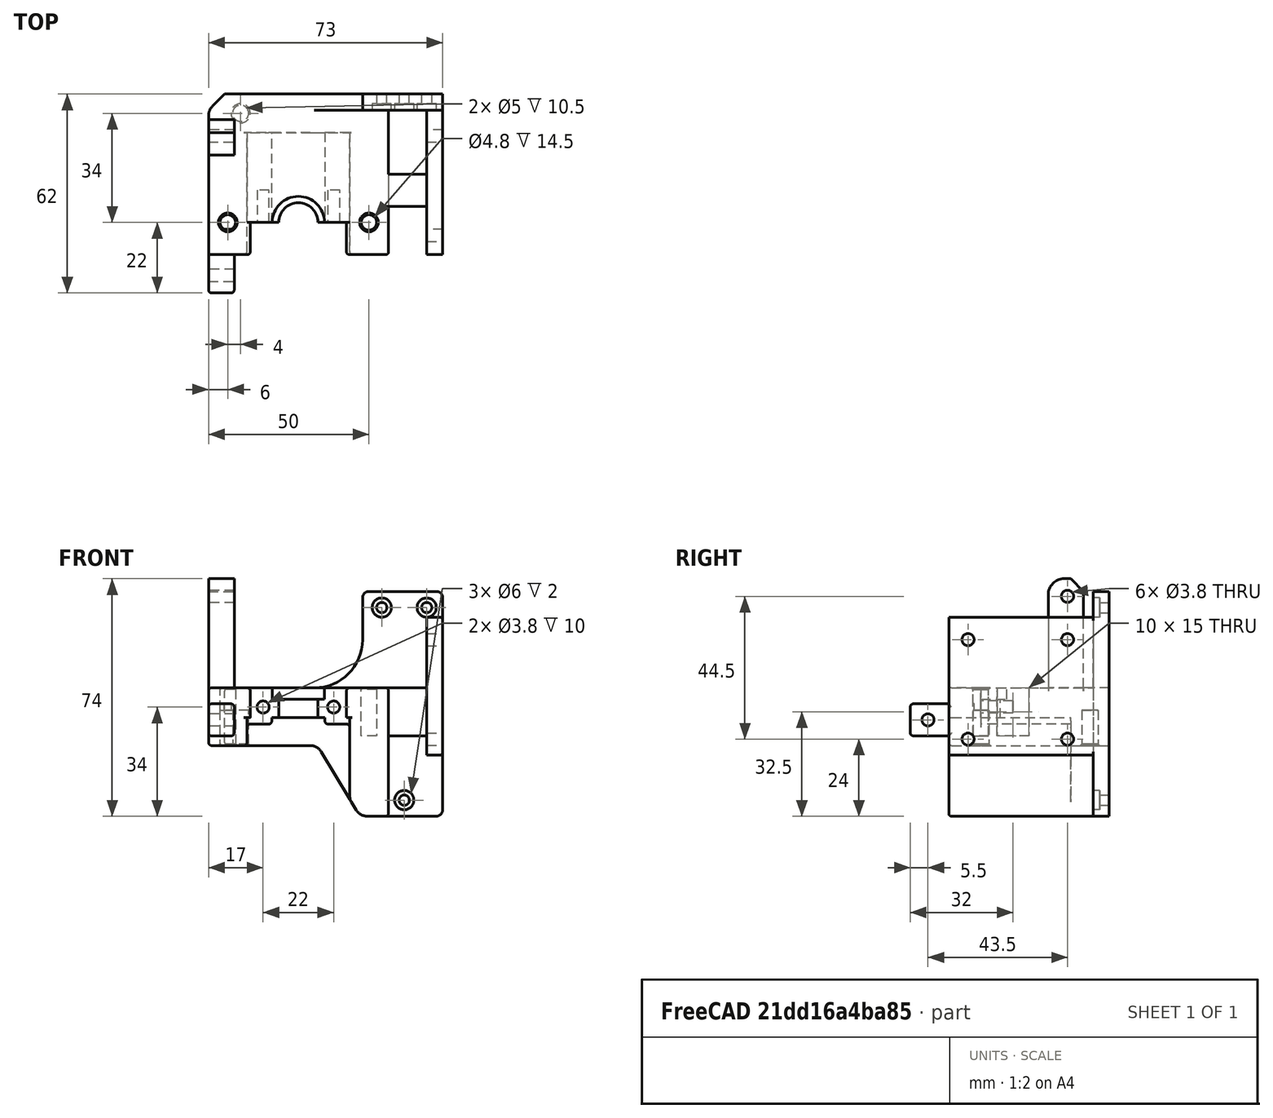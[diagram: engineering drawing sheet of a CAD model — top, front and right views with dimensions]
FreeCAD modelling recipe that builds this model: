
FCSTD DOCUMENT  (FreeCAD 0.19R)
Label: head8
License: All rights reserved
LicenseURL: http://en.wikipedia.org/wiki/All_rights_reserved
objects: Sketcher::SketchObject×19, PartDesign::Pocket×15, PartDesign::Fillet×15, PartDesign::Pad×4, PartDesign::Chamfer×4, PartDesign::Body×1, Mesh::Feature×1
note: 96 computed .brp shape members not serialized (recipe doc carries the construction recipe); baked Part::Feature solids carry a one-line shape summary decoded from their .brp

FEATURE [Sketcher::SketchObject] Sketch
  FullyConstrained = true
  MapMode = 5
  Support = -> [XY_Plane]
  sketch-geometry (5):
    g0: LineSegment StartX=0 StartY=0 StartZ=0 EndX=45 EndY=0 EndZ=0
    g1: LineSegment StartX=-28 StartY=0 StartZ=0 EndX=0 EndY=0 EndZ=0
    g2: LineSegment StartX=-28 StartY=0 StartZ=0 EndX=-28 EndY=-50 EndZ=0
    g3: LineSegment StartX=-28 StartY=-50 StartZ=0 EndX=45 EndY=-50 EndZ=0
    g4: LineSegment StartX=45 StartY=-50 StartZ=0 EndX=45 EndY=0 EndZ=0
  constraints (14):
    c: Coincident(g-1,g0)
    c: PointOnObject(g0,g-1)
    c: PointOnObject(g1,g-1)
    c: Coincident(g1,g0)
    c: Coincident(g1,g2)
    c: Vertical(g2)
    c: Coincident(g2,g3)
    c: Horizontal(g3)
    c: Coincident(g3,g4)
    c: Coincident(g4,g0)
    c: Vertical(g4)
    c: Distance(g4) = 50
    c: DistanceX(g0) = 45
    c: DistanceX(g1) = -28
FEATURE [PartDesign::Pad] Pad
  Direction = (1,1,1)
  Length = 70
  Length2 = 100
  Profile = -> Sketch
  Type = 0
FEATURE [Sketcher::SketchObject] Sketch001
  FullyConstrained = false
  MapMode = 5
  Placement = pos=(0,0,70) rot=(0,0,1;0rad)
  Support = -> [Pad]
  sketch-geometry (4):
    g0: LineSegment StartX=28.1122 StartY=-5 StartZ=0 EndX=40 EndY=-5 EndZ=0
    g1: LineSegment StartX=40 StartY=-5 StartZ=0 EndX=40 EndY=-51.78 EndZ=0
    g2: LineSegment StartX=40 StartY=-51.78 StartZ=0 EndX=28.1122 EndY=-51.78 EndZ=0
    g3: LineSegment StartX=28.1122 StartY=-51.78 StartZ=0 EndX=28.1122 EndY=-5 EndZ=0
  constraints (11):
    c: Coincident(g0,g1)
    c: Coincident(g1,g2)
    c: Coincident(g2,g3)
    c: Coincident(g3,g0)
    c: Horizontal(g0)
    c: Horizontal(g2)
    c: Vertical(g1)
    c: Vertical(g3)
    c: DistanceX(g0) = 40
    c: DistanceY(g1) = -51.78
    c: DistanceY(g0) = -5
FEATURE [PartDesign::Pocket] Pocket  label="BOBnotch"
  BaseFeature = -> Pad
  Length = 5
  Length2 = 100
  Profile = -> Sketch001
  Type = 1
FEATURE [Sketcher::SketchObject] Sketch002
  FullyConstrained = false
  MapMode = 5
  Placement = pos=(0,0,70) rot=(0,0,1;0rad)
  Support = -> [Pocket]
  sketch-geometry (6):
    g0: LineSegment StartX=30 StartY=-5 StartZ=0 EndX=30 EndY=-65.096 EndZ=0
    g1: LineSegment StartX=30 StartY=-65.096 StartZ=0 EndX=-40.7834 EndY=-65.096 EndZ=0
    g2: LineSegment StartX=-40.7834 StartY=-65.096 StartZ=0 EndX=-40.7834 EndY=12.9948 EndZ=0
    g3: LineSegment StartX=-40.7834 StartY=12.9948 StartZ=0 EndX=20 EndY=12.9948 EndZ=0
    g4: LineSegment StartX=20 StartY=12.9948 StartZ=0 EndX=20 EndY=-5 EndZ=0
    g5: LineSegment StartX=20 StartY=-5 StartZ=0 EndX=30 EndY=-5 EndZ=0
  constraints (15):
    c: Coincident(g0,g1)
    c: Coincident(g1,g2)
    c: Horizontal(g1)
    c: Vertical(g0)
    c: Vertical(g2)
    c: DistanceX(g0) = 30
    c: DistanceY(g0) = -5
    c: Coincident(g2,g3)
    c: Horizontal(g3)
    c: Coincident(g3,g4)
    c: Coincident(g4,g5)
    c: Coincident(g5,g0)
    c: Horizontal(g5)
    c: Vertical(g4)
    c: DistanceX(g3) = 20
FEATURE [PartDesign::Pocket] Pocket001  label="stepperplatform"
  BaseFeature = -> Pocket
  Length = 30
  Length2 = 100
  Profile = -> Sketch002
  Type = 0
FEATURE [Sketcher::SketchObject] Sketch003
  FullyConstrained = true
  MapMode = 5
  Placement = pos=(0,0,40) rot=(0,0,1;0rad)
  Support = -> [Pocket001]
  sketch-geometry (2):
    g0: Circle CenterX=-22 CenterY=-40 CenterZ=0 NormalX=0 NormalY=0 NormalZ=1 AngleXU=0 Radius=2.4
    g1: Circle CenterX=22 CenterY=-40 CenterZ=0 NormalX=0 NormalY=0 NormalZ=1 AngleXU=0 Radius=2.4
  constraints (5):
    c: Equal(g1,g0)
    c: Symmetric(g1,g0,g-2)
    c: Distance(g1,g0) = 44
    c: DistanceY(g0) = -40
    c: Diameter(g1) = 4.8
FEATURE [PartDesign::Pocket] Pocket002  label="steppermountholes"
  BaseFeature = -> Pocket001
  Length = 15
  Length2 = 100
  Profile = -> Sketch003
  Type = 0
FEATURE [Sketcher::SketchObject] Sketch004
  FullyConstrained = true
  MapMode = 5
  Placement = pos=(0,0,40) rot=(0,0,1;0rad)
  Support = -> [Pocket002]
  sketch-geometry (4):
    g0: ArcOfCircle CenterX=0 CenterY=-40 CenterZ=0 NormalX=0 NormalY=0 NormalZ=1 AngleXU=0 Radius=8.125 StartAngle=4e-16 EndAngle=3.14159
    g1: LineSegment StartX=8.125 StartY=-40 StartZ=0 EndX=8.125 EndY=-59.24 EndZ=0
    g2: LineSegment StartX=8.125 StartY=-59.24 StartZ=0 EndX=-8.125 EndY=-59.24 EndZ=0
    g3: LineSegment StartX=-8.125 StartY=-59.24 StartZ=0 EndX=-8.125 EndY=-40 EndZ=0
  constraints (11):
    c: PointOnObject(g0,g-2)
    c: Diameter(g0) = 16.25
    c: DistanceY(g0) = -40
    c: Coincident(g1,g2)
    c: Coincident(g2,g3)
    c: Horizontal(g2)
    c: Vertical(g3)
    c: Distance(g3) = 19.24
    c: Tangent(g3,g0) = 1.5708
    c: Tangent(g1,g0) = 1.5708
    c: Vertical(g1)
FEATURE [PartDesign::Pocket] Pocket003  label="hotendnotch001"
  BaseFeature = -> Pocket002
  Length = 3.5
  Length2 = 100
  Profile = -> Sketch004
  Type = 0
FEATURE [Sketcher::SketchObject] Sketch018
  FullyConstrained = true
  MapMode = 5
  Placement = pos=(0,0,36.5) rot=(0,0,1;0rad)
  sketch-geometry (4):
    g0: ArcOfCircle CenterX=0 CenterY=-40 CenterZ=0 NormalX=0 NormalY=0 NormalZ=1 AngleXU=0 Radius=6.1 StartAngle=-4e-14 EndAngle=3.14159
    g1: LineSegment StartX=6.1 StartY=-40 StartZ=0 EndX=6.1 EndY=-50 EndZ=0
    g2: LineSegment StartX=-6.1 StartY=-40 StartZ=0 EndX=-6.1 EndY=-50 EndZ=0
    g3: LineSegment StartX=6.1 StartY=-50 StartZ=0 EndX=-6.1 EndY=-50 EndZ=0
  constraints (11):
    c: PointOnObject(g0,g-2)
    c: Vertical(g1)
    c: Vertical(g2)
    c: Coincident(g3,g1)
    c: Coincident(g3,g2)
    c: Tangent(g1,g0) = 1.5708
    c: Tangent(g2,g0) = -1.5708
    c: DistanceY(g0) = -40
    c: Diameter(g0) = 12.2
    c: Horizontal(g3)
    c: Distance(g1) = 10
FEATURE [PartDesign::Pocket] Pocket004
  BaseFeature = -> Pocket003
  Length = 9
  Length2 = 100
  Profile = -> Sketch018
  Type = 0
FEATURE [Sketcher::SketchObject] Sketch021
  FullyConstrained = false
  MapMode = 5
  Placement = pos=(0,-50,0) rot=(1,0,0;1.5708rad)
  Support = -> [Pocket004]
  sketch-geometry (4):
    g0: LineSegment StartX=-15 StartY=43.4175 StartZ=0 EndX=15 EndY=43.4175 EndZ=0
    g1: LineSegment StartX=15 StartY=43.4175 StartZ=0 EndX=15 EndY=-9.74423 EndZ=0
    g2: LineSegment StartX=15 StartY=-9.74423 StartZ=0 EndX=-15 EndY=-9.74423 EndZ=0
    g3: LineSegment StartX=-15 StartY=-9.74423 StartZ=0 EndX=-15 EndY=43.4175 EndZ=0
  constraints (9):
    c: Coincident(g0,g1)
    c: Coincident(g1,g2)
    c: Coincident(g2,g3)
    c: Coincident(g3,g0)
    c: Horizontal(g2)
    c: Vertical(g1)
    c: Vertical(g3)
    c: Distance(g0,g0) = 30
    c: Symmetric(g0,g0,g-2)
FEATURE [PartDesign::Pocket] Pocket005  label="clampnotch"
  BaseFeature = -> Pocket004
  Length = 10
  Length2 = 100
  Profile = -> Sketch021
  Type = 0
FEATURE [Sketcher::SketchObject] Sketch022
  ExternalGeometry = -> [Pocket005]
  FullyConstrained = false
  MapMode = 5
  Placement = pos=(0,-50,0) rot=(1,0,0;1.5708rad)
  Support = -> [Pocket005]
  sketch-geometry (4):
    g0: LineSegment StartX=-16 StartY=30.7 StartZ=0 EndX=16 EndY=30.7 EndZ=0
    g1: LineSegment StartX=16 StartY=30.7 StartZ=0 EndX=16 EndY=-27.9602 EndZ=0
    g2: LineSegment StartX=16 StartY=-27.9602 StartZ=0 EndX=-16 EndY=-27.9602 EndZ=0
    g3: LineSegment StartX=-16 StartY=-27.9602 StartZ=0 EndX=-16 EndY=30.7 EndZ=0
  constraints (10):
    c: Coincident(g0,g1)
    c: Coincident(g1,g2)
    c: Coincident(g2,g3)
    c: Coincident(g3,g0)
    c: Horizontal(g2)
    c: Vertical(g1)
    c: Vertical(g3)
    c: Symmetric(g0,g0,g-2)
    c: Distance(g0) = 32
    c: Distance(g-5,g0) = 5.8
FEATURE [PartDesign::Pocket] Pocket006  label="fanNotch"
  BaseFeature = -> Pocket005
  Length = 38
  Length2 = 100
  Profile = -> Sketch022
  Type = 0
FEATURE [Sketcher::SketchObject] Sketch023
  ExternalGeometry = -> [Pocket006]
  FullyConstrained = true
  MapMode = 5
  Placement = pos=(0,-50,0) rot=(1,0,0;1.5708rad)
  Support = -> [Pocket006]
  sketch-geometry (4):
    g0: LineSegment StartX=-38.33 StartY=22 StartZ=0 EndX=6 EndY=22 EndZ=0
    g1: LineSegment StartX=6 StartY=22 StartZ=0 EndX=24 EndY=-8 EndZ=0
    g2: LineSegment StartX=24 StartY=-8 StartZ=0 EndX=-38.33 EndY=-8 EndZ=0
    g3: LineSegment StartX=-38.33 StartY=-8 StartZ=0 EndX=-38.33 EndY=22 EndZ=0
  constraints (12):
    c: Horizontal(g0)
    c: Coincident(g0,g1)
    c: Coincident(g1,g2)
    c: Horizontal(g2)
    c: Coincident(g2,g3)
    c: Coincident(g3,g0)
    c: DistanceX(g0) = 6
    c: DistanceX(g1) = 24
    c: DistanceY(g1) = -8
    c: Vertical(g3)
    c: Distance(g0) = 44.33
    c: Distance(g-3,g0) = 18
FEATURE [PartDesign::Pocket] Pocket007
  BaseFeature = -> Pocket006
  Length = 51
  Length2 = 100
  Profile = -> Sketch023
  Type = 0
FEATURE [Sketcher::SketchObject] Sketch008
  FullyConstrained = false
  MapMode = 5
  Placement = pos=(0,-50,0) rot=(1,0,0;1.5708rad)
  Support = -> [Pocket007]
  sketch-geometry (8):
    g0: LineSegment StartX=34.6158 StartY=72.6945 StartZ=0 EndX=53.669 EndY=72.6945 EndZ=0
    g1: LineSegment StartX=53.669 StartY=72.6945 StartZ=0 EndX=53.669 EndY=62 EndZ=0
    g2: LineSegment StartX=53.669 StartY=62 StartZ=0 EndX=34.6158 EndY=62 EndZ=0
    g3: LineSegment StartX=34.6158 StartY=62 StartZ=0 EndX=34.6158 EndY=72.6945 EndZ=0
    g4: LineSegment StartX=34.9227 StartY=19 StartZ=0 EndX=70.6727 EndY=19 EndZ=0
    g5: LineSegment StartX=70.6727 StartY=19 StartZ=0 EndX=70.6727 EndY=-17.1722 EndZ=0
    g6: LineSegment StartX=70.6727 StartY=-17.1722 StartZ=0 EndX=34.9227 EndY=-17.1722 EndZ=0
    g7: LineSegment StartX=34.9227 StartY=-17.1722 StartZ=0 EndX=34.9227 EndY=19 EndZ=0
  constraints (18):
    c: Coincident(g0,g1)
    c: Coincident(g1,g2)
    c: Coincident(g2,g3)
    c: Coincident(g3,g0)
    c: Horizontal(g0)
    c: Horizontal(g2)
    c: Vertical(g1)
    c: Vertical(g3)
    c: Coincident(g4,g5)
    c: Coincident(g5,g6)
    c: Coincident(g6,g7)
    c: Coincident(g7,g4)
    c: Horizontal(g4)
    c: Horizontal(g6)
    c: Vertical(g5)
    c: Vertical(g7)
    c: DistanceY(g2) = 62
    c: DistanceY(g4) = 19
FEATURE [PartDesign::Pocket] Pocket008
  BaseFeature = -> Pocket007
  Length = 45
  Length2 = 100
  Profile = -> Sketch008
  Type = 0
FEATURE [Sketcher::SketchObject] Sketch009
  FullyConstrained = true
  MapMode = 5
  Placement = pos=(45,0,0) rot=(0.57735,0.57735,0.57735;2.0944rad)
  Support = -> [Pocket008]
  sketch-geometry (5):
    g0: Circle CenterX=-44 CenterY=55 CenterZ=0 NormalX=0 NormalY=0 NormalZ=1 AngleXU=0 Radius=1.9
    g1: Circle CenterX=-13 CenterY=24 CenterZ=0 NormalX=0 NormalY=0 NormalZ=1 AngleXU=0 Radius=1.9
    g2: LineSegment StartX=-44 StartY=55 StartZ=0 EndX=-13 EndY=24 EndZ=0
    g3: Circle CenterX=-13 CenterY=55 CenterZ=0 NormalX=0 NormalY=0 NormalZ=1 AngleXU=0 Radius=1.9
    g4: Circle CenterX=-44 CenterY=24 CenterZ=0 NormalX=0 NormalY=0 NormalZ=1 AngleXU=0 Radius=1.9
  constraints (14):
    c: Coincident(g2,g0)
    c: Coincident(g2,g1)
    c: Angle(g2) = -0.785398
    c: DistanceX(g1) = -13
    c: DistanceY(g1) = 24
    c: Diameter(g4) = 3.8
    c: Equal(g4,g0)
    c: Equal(g4,g3)
    c: Equal(g4,g1)
    c: DistanceY(g4,g0) = 31
    c: DistanceX(g0,g3) = 31
    c: DistanceX(g4,g1) = 31
    c: DistanceY(g4) = 24
    c: DistanceY(g1,g3) = 31
FEATURE [PartDesign::Pocket] Pocket009  label="pcbholes"
  BaseFeature = -> Pocket008
  Length = 5
  Length2 = 100
  Profile = -> Sketch009
  Type = 0
FEATURE [Sketcher::SketchObject] Sketch015
  FullyConstrained = false
  MapMode = 5
  Placement = pos=(-28,0,0) rot=(0.57735,-0.57735,-0.57735;2.0944rad)
  Support = -> [Pocket009]
  sketch-geometry (8):
    g0: LineSegment StartX=8 StartY=74 StartZ=0 EndX=19 EndY=74 EndZ=0
    g1: LineSegment StartX=19 StartY=74 StartZ=0 EndX=19 EndY=35.8156 EndZ=0
    g2: LineSegment StartX=19 StartY=35.8156 StartZ=0 EndX=8 EndY=35.8156 EndZ=0
    g3: LineSegment StartX=8 StartY=35.8156 StartZ=0 EndX=8 EndY=74 EndZ=0
    g4: LineSegment StartX=42.1188 StartY=35 StartZ=0 EndX=62 EndY=35 EndZ=0
    g5: LineSegment StartX=62 StartY=35 StartZ=0 EndX=62 EndY=25 EndZ=0
    g6: LineSegment StartX=62 StartY=25 StartZ=0 EndX=42.1188 EndY=25 EndZ=0
    g7: LineSegment StartX=42.1188 StartY=25 StartZ=0 EndX=42.1188 EndY=35 EndZ=0
  constraints (22):
    c: Coincident(g0,g1)
    c: Coincident(g1,g2)
    c: Coincident(g2,g3)
    c: Coincident(g3,g0)
    c: Horizontal(g0)
    c: Horizontal(g2)
    c: Vertical(g1)
    c: Vertical(g3)
    c: DistanceY(g0) = 74
    c: Coincident(g4,g5)
    c: Coincident(g5,g6)
    c: Coincident(g6,g7)
    c: Coincident(g7,g4)
    c: Horizontal(g4)
    c: Horizontal(g6)
    c: Vertical(g5)
    c: Vertical(g7)
    c: DistanceX(g4) = 62
    c: DistanceY(g4) = 35
    c: DistanceY(g5) = 25
    c: DistanceX(g0) = 19
    c: DistanceX(g0) = 8
FEATURE [PartDesign::Pad] Pad001
  BaseFeature = -> Pocket009
  Direction = (1,1,1)
  Length = 8
  Length2 = 100
  Profile = -> Sketch015
  Reversed = true
  Type = 0
FEATURE [Sketcher::SketchObject] Sketch011
  FullyConstrained = true
  MapMode = 5
  Placement = pos=(-28,0,0) rot=(0.57735,-0.57735,-0.57735;2.0944rad)
  Support = -> [Pad001]
  sketch-geometry (3):
    g0: Circle CenterX=56.5 CenterY=30 CenterZ=0 NormalX=0 NormalY=0 NormalZ=1 AngleXU=0 Radius=1.9
    g1: Circle CenterX=13 CenterY=68.5 CenterZ=0 NormalX=0 NormalY=0 NormalZ=1 AngleXU=0 Radius=1.9
    g2: GeomPoint X=36 Y=48 Z=0
  constraints (8):
    c: Diameter(g0) = 3.8
    c: DistanceY(g0) = 30
    c: Diameter(g1) = 3.8
    c: DistanceX(g1) = 13
    c: DistanceY(g0,g2) = 18
    c: DistanceY(g2,g1) = 20.5
    c: DistanceX(g2,g0) = 20.5
    c: DistanceX(g1,g2) = 23
FEATURE [PartDesign::Pocket] Pocket010
  BaseFeature = -> Pad001
  Length = 10
  Length2 = 100
  Profile = -> Sketch011
  Type = 0
FEATURE [Sketcher::SketchObject] Sketch010
  FullyConstrained = true
  MapMode = 5
  Placement = pos=(0,0,0) rot=(0,0.707107,0.707107;3.14159rad)
  Support = -> [Pocket010]
  sketch-geometry (3):
    g0: Circle CenterX=-33 CenterY=5 CenterZ=0 NormalX=0 NormalY=0 NormalZ=1 AngleXU=0 Radius=1.6
    g1: Circle CenterX=-40 CenterY=65 CenterZ=0 NormalX=0 NormalY=0 NormalZ=1 AngleXU=0 Radius=1.6
    g2: Circle CenterX=-26 CenterY=65 CenterZ=0 NormalX=0 NormalY=0 NormalZ=1 AngleXU=0 Radius=1.6
  constraints (9):
    c: Diameter(g0) = 3.2
    c: Equal(g0,g2)
    c: Equal(g0,g1)
    c: DistanceX(g0) = -33
    c: Distance(g1,g2) = 14
    c: DistanceX(g2) = -26
    c: DistanceY(g0) = 5
    c: DistanceY(g2) = 65
    c: DistanceY(g1) = 65
FEATURE [PartDesign::Pocket] Pocket011
  BaseFeature = -> Pocket010
  Length = 7
  Length2 = 100
  Profile = -> Sketch010
  Type = 0
FEATURE [Sketcher::SketchObject] Sketch017
  FullyConstrained = false
  MapMode = 5
  Placement = pos=(0,-5,0) rot=(1,0,0;1.5708rad)
  Support = -> [Pocket011]
  sketch-geometry (3):
    g0: Circle CenterX=26 CenterY=65 CenterZ=0 NormalX=0 NormalY=0 NormalZ=1 AngleXU=0 Radius=3
    g1: Circle CenterX=33 CenterY=5 CenterZ=0 NormalX=0 NormalY=0 NormalZ=1 AngleXU=0 Radius=3
    g2: Circle CenterX=40 CenterY=65 CenterZ=0 NormalX=0 NormalY=0 NormalZ=1 AngleXU=0 Radius=3
  constraints (3):
    c: Diameter(g2) = 6
    c: Equal(g2,g1)
    c: Equal(g2,g0)
FEATURE [PartDesign::Pocket] Pocket012
  BaseFeature = -> Pocket011
  Length = 2
  Length2 = 100
  Profile = -> Sketch017
  Type = 0
FEATURE [Sketcher::SketchObject] Sketch013
  ExternalGeometry = -> [Pocket012]
  FullyConstrained = true
  MapMode = 5
  Placement = pos=(0,-40,5.3e-15) rot=(1,0,0;1.5708rad)
  Support = -> [Pocket012]
  sketch-geometry (2):
    g0: Circle CenterX=-11 CenterY=34 CenterZ=0 NormalX=0 NormalY=0 NormalZ=1 AngleXU=0 Radius=1.9
    g1: Circle CenterX=11 CenterY=34 CenterZ=0 NormalX=0 NormalY=0 NormalZ=1 AngleXU=0 Radius=1.9
  constraints (5):
    c: Symmetric(g1,g0,g-2)
    c: Distance(g1,g0) = 22
    c: Diameter(g1) = 3.8
    c: Equal(g1,g0)
    c: Distance(g1,g-3) = 6
FEATURE [PartDesign::Pocket] Pocket013
  BaseFeature = -> Pocket012
  Length = 10
  Length2 = 100
  Profile = -> Sketch013
  Type = 0
FEATURE [Sketcher::SketchObject] Sketch014
  FullyConstrained = true
  MapMode = 5
  Placement = pos=(45,0,0) rot=(0.57735,0.57735,0.57735;2.0944rad)
  Support = -> [Pocket013]
  sketch-geometry (4):
    g0: LineSegment StartX=-35 StartY=40 StartZ=0 EndX=-25 EndY=40 EndZ=0
    g1: LineSegment StartX=-25 StartY=40 StartZ=0 EndX=-25 EndY=25 EndZ=0
    g2: LineSegment StartX=-25 StartY=25 StartZ=0 EndX=-35 EndY=25 EndZ=0
    g3: LineSegment StartX=-35 StartY=25 StartZ=0 EndX=-35 EndY=40 EndZ=0
  constraints (12):
    c: Coincident(g0,g1)
    c: Coincident(g1,g2)
    c: Coincident(g2,g3)
    c: Coincident(g3,g0)
    c: Horizontal(g0)
    c: Horizontal(g2)
    c: Vertical(g1)
    c: Vertical(g3)
    c: Distance(g1) = 15
    c: Distance(g0) = 10
    c: DistanceX(g0) = -25
    c: DistanceY(g1) = 25
FEATURE [PartDesign::Pad] Pad002
  BaseFeature = -> Pocket013
  Direction = (1,1,1)
  Length = 18
  Length2 = 100
  Profile = -> Sketch014
  Reversed = true
  Type = 0
FEATURE [Sketcher::SketchObject] Sketch024
  FullyConstrained = false
  MapMode = 5
  Placement = pos=(0,6.8e-15,30.7) rot=(1,0,0;3.14159rad)
  Support = -> [Pad002]
  sketch-geometry (8):
    g0: LineSegment StartX=-16.5 StartY=40 StartZ=0 EndX=-8.25 EndY=40 EndZ=0
    g1: LineSegment StartX=-8.25 StartY=40 StartZ=0 EndX=-8.25 EndY=11.2448 EndZ=0
    g2: LineSegment StartX=-8.25 StartY=11.2448 StartZ=0 EndX=-16.5 EndY=11.2448 EndZ=0
    g3: LineSegment StartX=-16.5 StartY=11.2448 StartZ=0 EndX=-16.5 EndY=40 EndZ=0
    g4: LineSegment StartX=8.25 StartY=40 StartZ=0 EndX=16.5 EndY=40 EndZ=0
    g5: LineSegment StartX=16.5 StartY=40 StartZ=0 EndX=16.5 EndY=11.2448 EndZ=0
    g6: LineSegment StartX=16.5 StartY=11.2448 StartZ=0 EndX=8.25 EndY=11.2448 EndZ=0
    g7: LineSegment StartX=8.25 StartY=11.2448 StartZ=0 EndX=8.25 EndY=40 EndZ=0
  constraints (21):
    c: Coincident(g0,g1)
    c: Coincident(g1,g2)
    c: Coincident(g2,g3)
    c: Coincident(g3,g0)
    c: Horizontal(g0)
    c: Horizontal(g2)
    c: Vertical(g1)
    c: Vertical(g3)
    c: Coincident(g4,g5)
    c: Coincident(g5,g6)
    c: Coincident(g6,g7)
    c: Coincident(g7,g4)
    c: Horizontal(g6)
    c: Vertical(g5)
    c: Vertical(g7)
    c: Symmetric(g4,g0,g-2)
    c: Distance(g4,g0) = 16.5
    c: Symmetric(g4,g0,g-2)
    c: Equal(g1,g7)
    c: DistanceY(g4) = 40
    c: Distance(g4,g0) = 33
FEATURE [PartDesign::Pad] Pad003
  BaseFeature = -> Pad002
  Direction = (1,1,1)
  Length = 2
  Length2 = 100
  Profile = -> Sketch024
  Type = 0
FEATURE [PartDesign::Chamfer] Chamfer
  Angle = 45
  Base = -> Pad003 [Edge150]
  BaseFeature = -> Pad003
  ChamferType = 0
  FlipDirection = false
  Size = 4
  Size2 = 1
  SupportTransform = false
FEATURE [PartDesign::Fillet] Fillet
  Base = -> Chamfer [Edge40]
  BaseFeature = -> Chamfer
  Radius = 5
  SupportTransform = false
FEATURE [PartDesign::Chamfer] Chamfer001
  Angle = 45
  Base = -> Fillet [Edge50]
  BaseFeature = -> Fillet
  ChamferType = 0
  FlipDirection = false
  Size = 5
  Size2 = 1
  SupportTransform = false
FEATURE [PartDesign::Fillet] Fillet001
  Base = -> Chamfer001 [Edge29]
  BaseFeature = -> Chamfer001
  Radius = 4
  SupportTransform = false
FEATURE [PartDesign::Fillet] Fillet002
  Base = -> Fillet001 [Edge7]
  BaseFeature = -> Fillet001
  Radius = 15
  SupportTransform = false
FEATURE [PartDesign::Fillet] Fillet003
  Base = -> Fillet002 [Edge17,Edge58,Edge139,Edge55,Edge120,Edge124,Edge16,Edge21]
  BaseFeature = -> Fillet002
  Radius = 1
  SupportTransform = false
FEATURE [PartDesign::Fillet] Fillet004
  Base = -> Fillet003 [Edge18]
  BaseFeature = -> Fillet003
  Radius = 1
  SupportTransform = false
FEATURE [PartDesign::Fillet] Fillet005
  Base = -> Fillet004 [Edge249,Edge262]
  BaseFeature = -> Fillet004
  Radius = 1
  SupportTransform = false
FEATURE [PartDesign::Fillet] Fillet006
  Base = -> Fillet005 [Edge9,Edge86]
  BaseFeature = -> Fillet005
  Radius = 1
  SupportTransform = false
FEATURE [PartDesign::Fillet] Fillet007
  Base = -> Fillet006 [Edge252,Edge251,Edge254,Edge257]
  BaseFeature = -> Fillet006
  Radius = 1
  SupportTransform = false
FEATURE [PartDesign::Fillet] Fillet008
  Base = -> Fillet007 [Edge84]
  BaseFeature = -> Fillet007
  Radius = 1
  SupportTransform = false
FEATURE [PartDesign::Fillet] Fillet009
  Base = -> Fillet008 [Edge190,Edge81,Edge191]
  BaseFeature = -> Fillet008
  Radius = 4
  SupportTransform = false
FEATURE [PartDesign::Fillet] Fillet010
  Base = -> Fillet009 [Edge74,Edge84,Edge98]
  BaseFeature = -> Fillet009
  Radius = 2
  SupportTransform = false
FEATURE [PartDesign::Fillet] Fillet011
  Base = -> Fillet010 [Face115]
  BaseFeature = -> Fillet010
  Radius = 1
  SupportTransform = false
FEATURE [PartDesign::Fillet] Fillet012
  Base = -> Fillet011 [Edge161]
  BaseFeature = -> Fillet011
  Radius = 0.8
  SupportTransform = false
FEATURE [PartDesign::Fillet] Fillet013
  Base = -> Fillet012 [Edge97]
  BaseFeature = -> Fillet012
  Radius = 0.8
  SupportTransform = false
FEATURE [PartDesign::Fillet] Fillet014
  Base = -> Fillet013 [Edge141]
  BaseFeature = -> Fillet013
  Radius = 1
  SupportTransform = false
FEATURE [Sketcher::SketchObject] Sketch025
  FullyConstrained = true
  MapMode = 5
  Placement = pos=(0,4.9e-15,22) rot=(1,0,0;3.14159rad)
  Support = -> [Fillet014]
  sketch-geometry (2):
    g0: Circle CenterX=-22 CenterY=40 CenterZ=0 NormalX=0 NormalY=0 NormalZ=1 AngleXU=0 Radius=2.5
    g1: Circle CenterX=-18 CenterY=6 CenterZ=0 NormalX=0 NormalY=0 NormalZ=1 AngleXU=0 Radius=2.5
  constraints (6):
    c: Diameter(g0) = 5
    c: Equal(g0,g1)
    c: DistanceX(g0) = -22
    c: DistanceX(g1) = -18
    c: DistanceY(g1) = 6
    c: DistanceY(g0) = 40
FEATURE [PartDesign::Pocket] Pocket014
  BaseFeature = -> Fillet014
  Length = 11
  Length2 = 100
  Profile = -> Sketch025
  Type = 0
FEATURE [PartDesign::Chamfer] Chamfer002
  Angle = 45
  Base = -> Pocket014 [Edge83,Edge84]
  BaseFeature = -> Pocket014
  ChamferType = 0
  FlipDirection = false
  Size = 0.5
  Size2 = 1
  SupportTransform = false
FEATURE [PartDesign::Chamfer] Chamfer003
  Angle = 45
  Base = -> Chamfer002 [Edge199,Edge198]
  BaseFeature = -> Chamfer002
  ChamferType = 0
  FlipDirection = false
  Size = 0.5
  Size2 = 1
  SupportTransform = false
FEATURE [PartDesign::Body] Body
  Group = -> [Sketch,Pad,Sketch001,Pocket,Sketch002,Pocket001,Sketch003,Pocket002,Sketch004,Pocket003,Sketch008,Sketch009,Sketch010,Sketch011,Sketch013,Sketch014,Sketch015,Sketch017,Sketch018,Pocket004,Sketch021,Pocket005,Sketch022,Pocket006,Sketch023,Pocket007,Pocket008,Pocket009,Pad001,Pocket010,Pocket011,Pocket012,Pocket013,Pad002,Sketch024,Pad003,Chamfer,Fillet,Chamfer001,Fillet001,Fillet002,Fillet003,+15 more]
  Origin = -> Origin
  Tip = -> Chamfer003
FEATURE [Mesh::Feature] Mesh  label="Chamfer003 (Meshed)"
